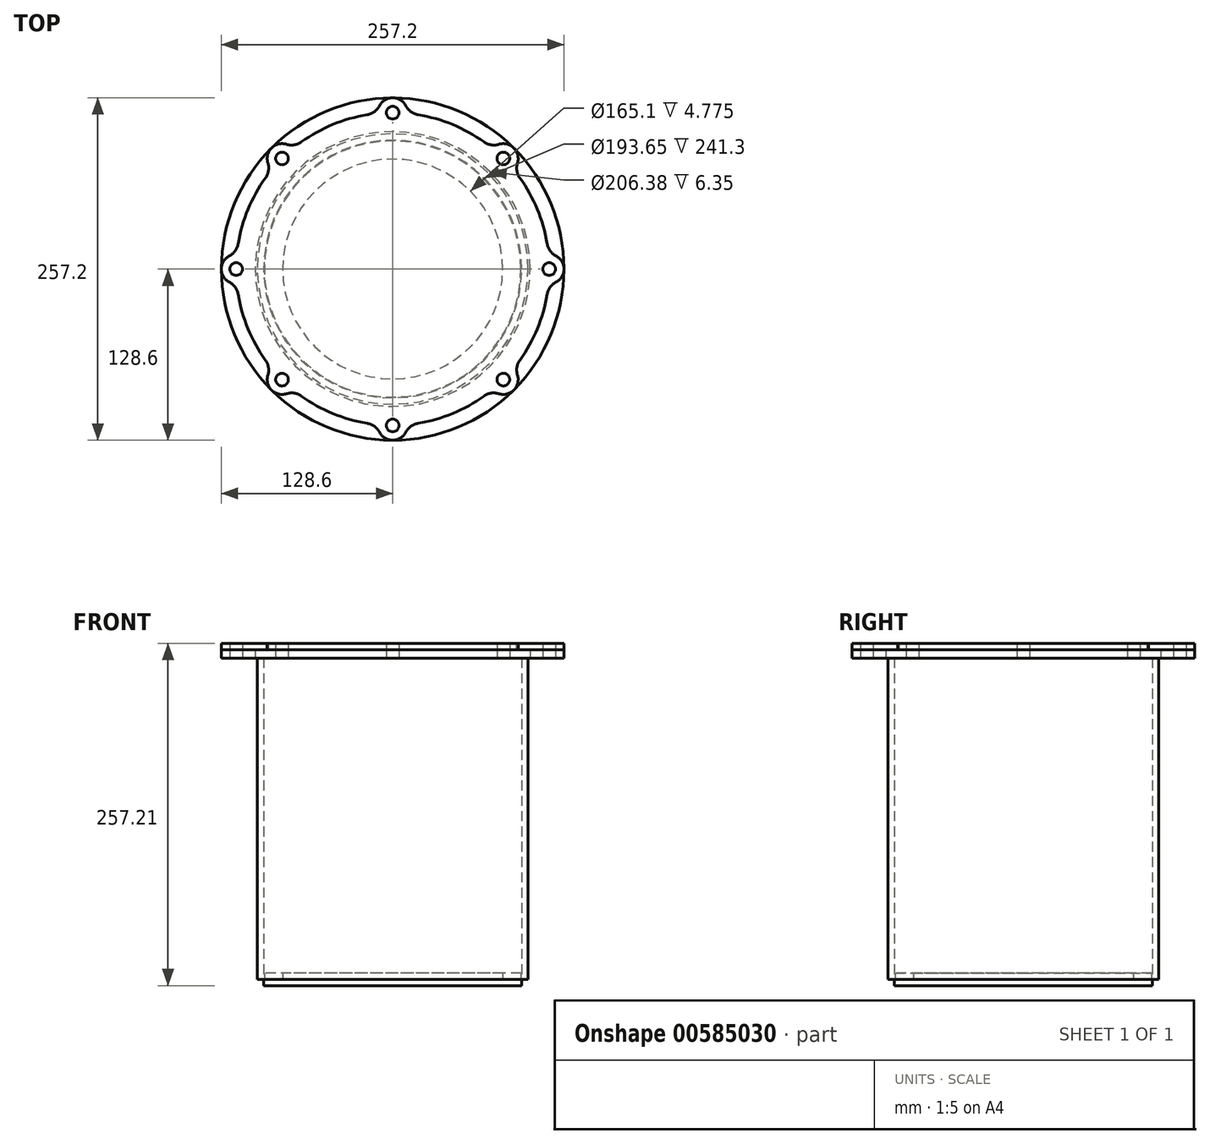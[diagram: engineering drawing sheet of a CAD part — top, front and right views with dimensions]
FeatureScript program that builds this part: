
annotation { "Feature Type Name" : "Feature", "Feature Type Description" : "" }
export const myFeature = defineFeature(function(context is Context, id is Id, definition is map)
    precondition{}
    {
        {
            var Q0;
            Q0=qCreatedBy(makeId("Top.planeOp"),FACE);
            var sketch = newSketch(context, id + "F0", { "sketchPlane" : qUnion([Q0])});
            skCircle(sketch, "E0", {"center": v(0, 0) * mm, "radius": 101.6 * mm});
            skCircle(sketch, "E1.0", {"center": v(0, 0) * mm, "radius": 96.82 * mm});
            skSolve(sketch);
        }
        {
            var Q0;
            Q0 = qSketchRegion(id + "F0", true);
            extrude(context, id + "F1", {"entities" : qUnion([Q0]), "depth" : 241.3 * mm, "offsetDistance" : 25.4 * mm});
        }
        {
            var Q0;
            Q0=qCreatedBy(makeId("Top.planeOp"),FACE);
            var sketch = newSketch(context, id + "F2", { "sketchPlane" : qUnion([Q0])});
            skCircle(sketch, "E2", {"center": v(0, 0) * mm, "radius": 96.27 * mm});
            skCircle(sketch, "E3", {"center": v(0, 0) * mm, "radius": 82.55 * mm});
            skSolve(sketch);
        }
        {
            var Q0;
            Q0 = qSketchRegion(id + "F2", true);
            extrude(context, id + "F3", {"entities" : qUnion([Q0]), "operationType" : NewBodyOperationType.ADD, "depth" : 4.78 * mm, "offsetDistance" : 25.4 * mm});
        }
        {
            var Q0;
            Q0=makeQuery(id+"F1.opExtrude","CAP_FACE",FACE,{"disambiguationData":[OSD([sQuery(id+"F0.wireOp",EDGE,"E0"),sQuery(id+"F0.wireOp",EDGE,"E1.0")])],"isStart":false});
            var sketch = newSketch(context, id + "F4", { "sketchPlane" : qUnion([Q0])});
            skCircle(sketch, "E4", {"center": v(0, 0) * mm, "radius": 103.19 * mm});
            skCircle(sketch, "E5", {"center": v(0, 0) * mm, "radius": 128.59 * mm});
            skCircle(sketch, "E6", {"center": v(0, 0) * mm, "radius": 117.48 * mm, "construction": true});
            skLineSegment(sketch, "E7", {"start": v(0, 0) * mm, "end": v(0, 117.48) * mm, "construction": true});
            skCircle(sketch, "E8", {"center": v(0, 117.48) * mm, "radius": 4.76 * mm});
            skCircle(sketch, "E9.1.0", {"center": v(-83.07, 83.07) * mm, "radius": 4.76 * mm});
            skCircle(sketch, "E9.2.0", {"center": v(-117.48, 0) * mm, "radius": 4.76 * mm});
            skCircle(sketch, "E9.3.0", {"center": v(-83.07, -83.07) * mm, "radius": 4.76 * mm});
            skCircle(sketch, "E9.4.0", {"center": v(0, -117.48) * mm, "radius": 4.76 * mm});
            skCircle(sketch, "E9.5.0", {"center": v(83.07, -83.07) * mm, "radius": 4.76 * mm});
            skCircle(sketch, "E9.6.0", {"center": v(117.48, 0) * mm, "radius": 4.76 * mm});
            skCircle(sketch, "E9.7.0", {"center": v(83.07, 83.07) * mm, "radius": 4.76 * mm});
            skSolve(sketch);
        }
        {
            var Q0;
            Q0 = qSketchRegion(id + "F4", true);
            extrude(context, id + "F5", {"entities" : qUnion([Q0]), "depth" : 6.35 * mm, "offsetDistance" : 25.4 * mm});
        }
        {
            var Q0;
            Q0=makeQuery(id+"F5.opExtrude","CAP_FACE",FACE,{"disambiguationData":[OSD([sQuery(id+"F4.wireOp",EDGE,"E4"),sQuery(id+"F4.wireOp",EDGE,"E5"),sQuery(id+"F4.wireOp",EDGE,"E8"),sQuery(id+"F4.wireOp",EDGE,"E9.1.0"),sQuery(id+"F4.wireOp",EDGE,"E9.2.0"),sQuery(id+"F4.wireOp",EDGE,"E9.3.0"),sQuery(id+"F4.wireOp",EDGE,"E9.4.0"),sQuery(id+"F4.wireOp",EDGE,"E9.5.0"),sQuery(id+"F4.wireOp",EDGE,"E9.6.0"),sQuery(id+"F4.wireOp",EDGE,"E9.7.0")])],"isStart":false});
            var sketch = newSketch(context, id + "F6", { "sketchPlane" : qUnion([Q0])});
            skCircle(sketch, "E10", {"center": v(0, 0) * mm, "radius": 128.59 * mm, "construction": true});
            skLineSegment(sketch, "E11", {"start": v(0, 0) * mm, "end": v(0, 117.48) * mm, "construction": true});
            skCircle(sketch, "E12", {"center": v(0, 117.48) * mm, "radius": 4.76 * mm});
            skCircle(sketch, "E13.1.0", {"center": v(-83.07, 83.07) * mm, "radius": 4.76 * mm});
            skCircle(sketch, "E13.2.0", {"center": v(-117.48, 0) * mm, "radius": 4.76 * mm});
            skCircle(sketch, "E13.3.0", {"center": v(-83.07, -83.07) * mm, "radius": 4.76 * mm});
            skCircle(sketch, "E13.4.0", {"center": v(0, -117.48) * mm, "radius": 4.76 * mm});
            skCircle(sketch, "E13.5.0", {"center": v(83.07, -83.07) * mm, "radius": 4.76 * mm});
            skCircle(sketch, "E13.6.0", {"center": v(117.48, 0) * mm, "radius": 4.76 * mm});
            skCircle(sketch, "E13.7.0", {"center": v(83.07, 83.07) * mm, "radius": 4.76 * mm});
            skArc(sketch, "E14", {"start": v(11.11, 116.95) * mm, "mid": v(0, 128.6) * mm, "end": v(-11.11, 116.95) * mm});
            skArc(sketch, "E15.1.0", {"start": v(-74.84, 90.55) * mm, "mid": v(-90.93, 90.93) * mm, "end": v(-90.55, 74.84) * mm});
            skArc(sketch, "E15.2.0", {"start": v(-116.95, 11.11) * mm, "mid": v(-128.6, 0) * mm, "end": v(-116.95, -11.11) * mm});
            skArc(sketch, "E15.3.0", {"start": v(-90.55, -74.84) * mm, "mid": v(-90.93, -90.93) * mm, "end": v(-74.84, -90.55) * mm});
            skArc(sketch, "E15.4.0", {"start": v(-11.11, -116.95) * mm, "mid": v(0, -128.6) * mm, "end": v(11.11, -116.95) * mm});
            skArc(sketch, "E15.5.0", {"start": v(74.84, -90.55) * mm, "mid": v(90.93, -90.93) * mm, "end": v(90.55, -74.84) * mm});
            skArc(sketch, "E15.6.0", {"start": v(116.95, -11.11) * mm, "mid": v(128.6, 0) * mm, "end": v(116.95, 11.11) * mm});
            skArc(sketch, "E15.7.0", {"start": v(90.55, 74.84) * mm, "mid": v(90.93, 90.93) * mm, "end": v(74.84, 90.55) * mm});
            skArc(sketch, "E16", {"start": v(74.84, 90.55) * mm, "mid": v(44.96, 108.53) * mm, "end": v(11.11, 116.95) * mm});
            skArc(sketch, "E17.1.0", {"start": v(-11.11, 116.95) * mm, "mid": v(-44.96, 108.53) * mm, "end": v(-74.84, 90.55) * mm});
            skArc(sketch, "E17.2.0", {"start": v(-90.55, 74.84) * mm, "mid": v(-108.53, 44.96) * mm, "end": v(-116.95, 11.11) * mm});
            skArc(sketch, "E17.3.0", {"start": v(-116.95, -11.11) * mm, "mid": v(-108.53, -44.96) * mm, "end": v(-90.55, -74.84) * mm});
            skArc(sketch, "E17.4.0", {"start": v(-74.84, -90.55) * mm, "mid": v(-44.96, -108.53) * mm, "end": v(-11.11, -116.95) * mm});
            skArc(sketch, "E17.5.0", {"start": v(11.11, -116.95) * mm, "mid": v(44.96, -108.53) * mm, "end": v(74.84, -90.55) * mm});
            skArc(sketch, "E17.6.0", {"start": v(90.55, -74.84) * mm, "mid": v(108.53, -44.96) * mm, "end": v(116.95, -11.11) * mm});
            skArc(sketch, "E17.7.0", {"start": v(116.95, 11.11) * mm, "mid": v(108.53, 44.96) * mm, "end": v(90.55, 74.84) * mm});
            skSolve(sketch);
        }
        {
            var Q0;
            Q0=makeQuery(id+"F1.opExtrude","CAP_FACE",FACE,{"disambiguationData":[OSD([sQuery(id+"F0.wireOp",EDGE,"E0"),sQuery(id+"F0.wireOp",EDGE,"E1.0")])],"isStart":true});
            var sketch = newSketch(context, id + "F7", { "sketchPlane" : qUnion([Q0])});
            skCircle(sketch, "E18", {"center": v(0, 0) * mm, "radius": 96.84 * mm});
            skSolve(sketch);
        }
        {
            var Q0;
            Q0=makeQuery(id+"F7.imprint","IMPRINT",FACE,{"disambiguationData":[TD([[makeQuery(id+"F7.imprint","IMPRINT",EDGE,{"derivedFrom":makeQuery(id+"F1.opExtrude","CAP_EDGE",EDGE,{"disambiguationData":[OSD([sQuery(id+"F0.wireOp",EDGE,"E1.0")])],"isStart":true})}),-1.0]])]});
            extrude(context, id + "F8", {"entities" : qUnion([Q0]), "depth" : 4.78 * mm, "offsetDistance" : 25.4 * mm});
        }
        {
            var Q0;
            Q0 = qSketchRegion(id + "F6", true);
            extrude(context, id + "F9", {"entities" : qUnion([Q0]), "depth" : 4.78 * mm, "offsetDistance" : 25.4 * mm});
        }
        {
            var Q0;
            Q0=makeQuery(id+"F9.opExtrude","SWEPT_EDGE",EDGE,{"disambiguationData":[OSD([sQuery(id+"F6.wireOp",EDGE,"E15.7.0"),sQuery(id+"F6.wireOp",EDGE,"E16")])]});
            var Q1;
            Q1=makeQuery(id+"F9.opExtrude","SWEPT_EDGE",EDGE,{"disambiguationData":[OSD([sQuery(id+"F6.wireOp",EDGE,"E15.7.0"),sQuery(id+"F6.wireOp",EDGE,"E17.7.0")])]});
            var Q2;
            Q2=makeQuery(id+"F9.opExtrude","SWEPT_EDGE",EDGE,{"disambiguationData":[OSD([sQuery(id+"F6.wireOp",EDGE,"E14"),sQuery(id+"F6.wireOp",EDGE,"E16")])]});
            var Q3;
            Q3=makeQuery(id+"F9.opExtrude","SWEPT_EDGE",EDGE,{"disambiguationData":[OSD([sQuery(id+"F6.wireOp",EDGE,"E14"),sQuery(id+"F6.wireOp",EDGE,"E17.1.0")])]});
            var Q4;
            Q4=makeQuery(id+"F9.opExtrude","SWEPT_EDGE",EDGE,{"disambiguationData":[OSD([sQuery(id+"F6.wireOp",EDGE,"E15.1.0"),sQuery(id+"F6.wireOp",EDGE,"E17.1.0")])]});
            var Q5;
            Q5=makeQuery(id+"F9.opExtrude","SWEPT_EDGE",EDGE,{"disambiguationData":[OSD([sQuery(id+"F6.wireOp",EDGE,"E15.1.0"),sQuery(id+"F6.wireOp",EDGE,"E17.2.0")])]});
            var Q6;
            Q6=makeQuery(id+"F9.opExtrude","SWEPT_EDGE",EDGE,{"disambiguationData":[OSD([sQuery(id+"F6.wireOp",EDGE,"E15.2.0"),sQuery(id+"F6.wireOp",EDGE,"E17.2.0")])]});
            var Q7;
            Q7=makeQuery(id+"F9.opExtrude","SWEPT_EDGE",EDGE,{"disambiguationData":[OSD([sQuery(id+"F6.wireOp",EDGE,"E15.2.0"),sQuery(id+"F6.wireOp",EDGE,"E17.3.0")])]});
            var Q8;
            Q8=makeQuery(id+"F9.opExtrude","SWEPT_EDGE",EDGE,{"disambiguationData":[OSD([sQuery(id+"F6.wireOp",EDGE,"E15.3.0"),sQuery(id+"F6.wireOp",EDGE,"E17.3.0")])]});
            var Q9;
            Q9=makeQuery(id+"F9.opExtrude","SWEPT_EDGE",EDGE,{"disambiguationData":[OSD([sQuery(id+"F6.wireOp",EDGE,"E15.3.0"),sQuery(id+"F6.wireOp",EDGE,"E17.4.0")])]});
            var Q10;
            Q10=makeQuery(id+"F9.opExtrude","SWEPT_EDGE",EDGE,{"disambiguationData":[OSD([sQuery(id+"F6.wireOp",EDGE,"E15.4.0"),sQuery(id+"F6.wireOp",EDGE,"E17.4.0")])]});
            var Q11;
            Q11=makeQuery(id+"F9.opExtrude","SWEPT_EDGE",EDGE,{"disambiguationData":[OSD([sQuery(id+"F6.wireOp",EDGE,"E15.5.0"),sQuery(id+"F6.wireOp",EDGE,"E17.5.0")])]});
            var Q12;
            Q12=makeQuery(id+"F9.opExtrude","SWEPT_EDGE",EDGE,{"disambiguationData":[OSD([sQuery(id+"F6.wireOp",EDGE,"E15.5.0"),sQuery(id+"F6.wireOp",EDGE,"E17.6.0")])]});
            var Q13;
            Q13=makeQuery(id+"F9.opExtrude","SWEPT_EDGE",EDGE,{"disambiguationData":[OSD([sQuery(id+"F6.wireOp",EDGE,"E15.6.0"),sQuery(id+"F6.wireOp",EDGE,"E17.7.0")])]});
            var Q14;
            Q14=makeQuery(id+"F9.opExtrude","SWEPT_EDGE",EDGE,{"disambiguationData":[OSD([sQuery(id+"F6.wireOp",EDGE,"E15.6.0"),sQuery(id+"F6.wireOp",EDGE,"E17.6.0")])]});
            var Q15;
            Q15=makeQuery(id+"F9.opExtrude","SWEPT_EDGE",EDGE,{"disambiguationData":[OSD([sQuery(id+"F6.wireOp",EDGE,"E15.4.0"),sQuery(id+"F6.wireOp",EDGE,"E17.5.0")])]});
            fillet(context, id + "F10", {"entities" : qUnion([Q0, Q1, Q2, Q3, Q4, Q5, Q6, Q7, Q8, Q9, Q10, Q11, Q12, Q13, Q14, Q15]), "tangentPropagation" : true, "radius" : 12.7 * mm, "defaultsChanged" : true, "vertexSettings" : [], "allowEdgeOverflow" : false});
        }
    });
